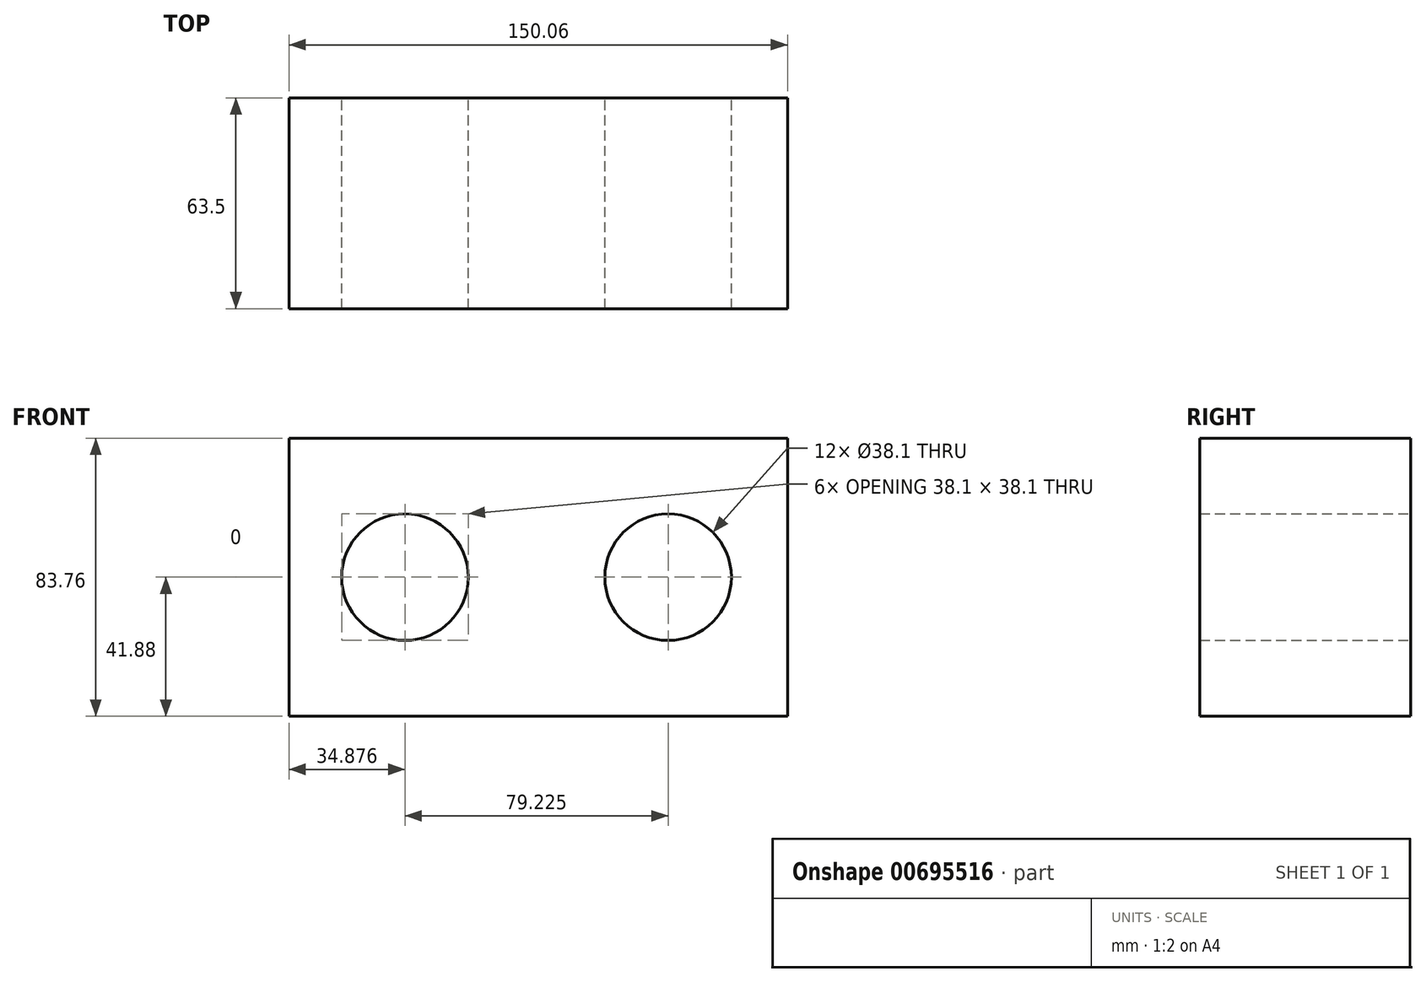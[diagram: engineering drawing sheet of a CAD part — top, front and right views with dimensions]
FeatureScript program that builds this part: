
annotation { "Feature Type Name" : "Feature", "Feature Type Description" : "" }
export const myFeature = defineFeature(function(context is Context, id is Id, definition is map)
    precondition{}
    {
        {
            var Q0;
            Q0=qCreatedBy(makeId("Front.planeOp"),FACE);
            var sketch = newSketch(context, id + "F0", { "sketchPlane" : qUnion([Q0])});
            skLineSegment(sketch, "E0.bottom", {"start": v(75.03, -41.88) * mm, "end": v(-75.03, -41.88) * mm});
            skLineSegment(sketch, "E0.top", {"start": v(75.03, 41.88) * mm, "end": v(-75.03, 41.88) * mm});
            skLineSegment(sketch, "E0.left", {"start": v(75.03, -41.88) * mm, "end": v(75.03, 41.88) * mm});
            skLineSegment(sketch, "E0.right", {"start": v(-75.03, -41.88) * mm, "end": v(-75.03, 41.88) * mm});
            skPoint(sketch, "E0.middle", {"position": v(0, 0) * mm});
            skSolve(sketch);
        }
        {
            var Q0;
            Q0=makeQuery(id+"F0.imprint","IMPRINT",FACE,{"disambiguationData":[TD([[makeQuery(id+"F0.imprint","IMPRINT",EDGE,{"derivedFrom":sQuery(id+"F0.wireOp",EDGE,"E0.bottom")}),-1.0]])]});
            extrude(context, id + "F1", {"entities" : qUnion([Q0]), "depth" : 63.5 * mm, "offsetDistance" : 25.4 * mm});
        }
        {
            var Q0;
            Q0=makeQuery(id+"F1.opExtrude","CAP_FACE",FACE,{"disambiguationData":[OSD([sQuery(id+"F0.wireOp",EDGE,"E0.bottom"),sQuery(id+"F0.wireOp",EDGE,"E0.top"),sQuery(id+"F0.wireOp",EDGE,"E0.left"),sQuery(id+"F0.wireOp",EDGE,"E0.right")])],"isStart":true});
            var sketch = newSketch(context, id + "F2", { "sketchPlane" : qUnion([Q0])});
            skPoint(sketch, "E1", {"position": v(-39.07, 0) * mm});
            skSolve(sketch);
        }
        {
            var Q0;
            Q0=sQuery(id+"F2.wireOp",VERTEX,"E1");
            var Q1;
            Q1=makeQuery(id+"F1.opExtrude","SWEPT_BODY",BODY,{"disambiguationData":[OSD([sQuery(id+"F0.wireOp",EDGE,"E0.bottom"),sQuery(id+"F0.wireOp",EDGE,"E0.top"),sQuery(id+"F0.wireOp",EDGE,"E0.left"),sQuery(id+"F0.wireOp",EDGE,"E0.right")])]});
            hole(context, id + "F3", {"style" : HoleStyle.SIMPLE, "endStyle" : HoleEndStyle.THROUGH, "holeDiameter" : 38.1 * mm, "majorDiameter" : 6.35 * mm, "isTappedThrough" : true, "tappedDepth" : 12.7 * mm, "tapClearance" : 3, "locations" : qUnion([Q0]), "scope" : qUnion([Q1])});
        }
        {
            var Q0;
            Q0=makeQuery(id+"F1.opExtrude","CAP_FACE",FACE,{"disambiguationData":[OSD([sQuery(id+"F0.wireOp",EDGE,"E0.bottom"),sQuery(id+"F0.wireOp",EDGE,"E0.top"),sQuery(id+"F0.wireOp",EDGE,"E0.left"),sQuery(id+"F0.wireOp",EDGE,"E0.right")])],"isStart":true});
            var sketch = newSketch(context, id + "F4", { "sketchPlane" : qUnion([Q0])});
            skPoint(sketch, "E2", {"position": v(40.15, 0) * mm});
            skSolve(sketch);
        }
        {
            var Q0;
            Q0=sQuery(id+"F4.wireOp",VERTEX,"E2");
            var Q1;
            Q1=makeQuery(id+"F1.opExtrude","SWEPT_BODY",BODY,{"disambiguationData":[OSD([sQuery(id+"F0.wireOp",EDGE,"E0.bottom"),sQuery(id+"F0.wireOp",EDGE,"E0.top"),sQuery(id+"F0.wireOp",EDGE,"E0.left"),sQuery(id+"F0.wireOp",EDGE,"E0.right")])]});
            hole(context, id + "F5", {"style" : HoleStyle.SIMPLE, "endStyle" : HoleEndStyle.THROUGH, "holeDiameter" : 38.1 * mm, "majorDiameter" : 6.35 * mm, "isTappedThrough" : true, "tappedDepth" : 12.7 * mm, "tapClearance" : 3, "locations" : qUnion([Q0]), "scope" : qUnion([Q1])});
        }
    });
